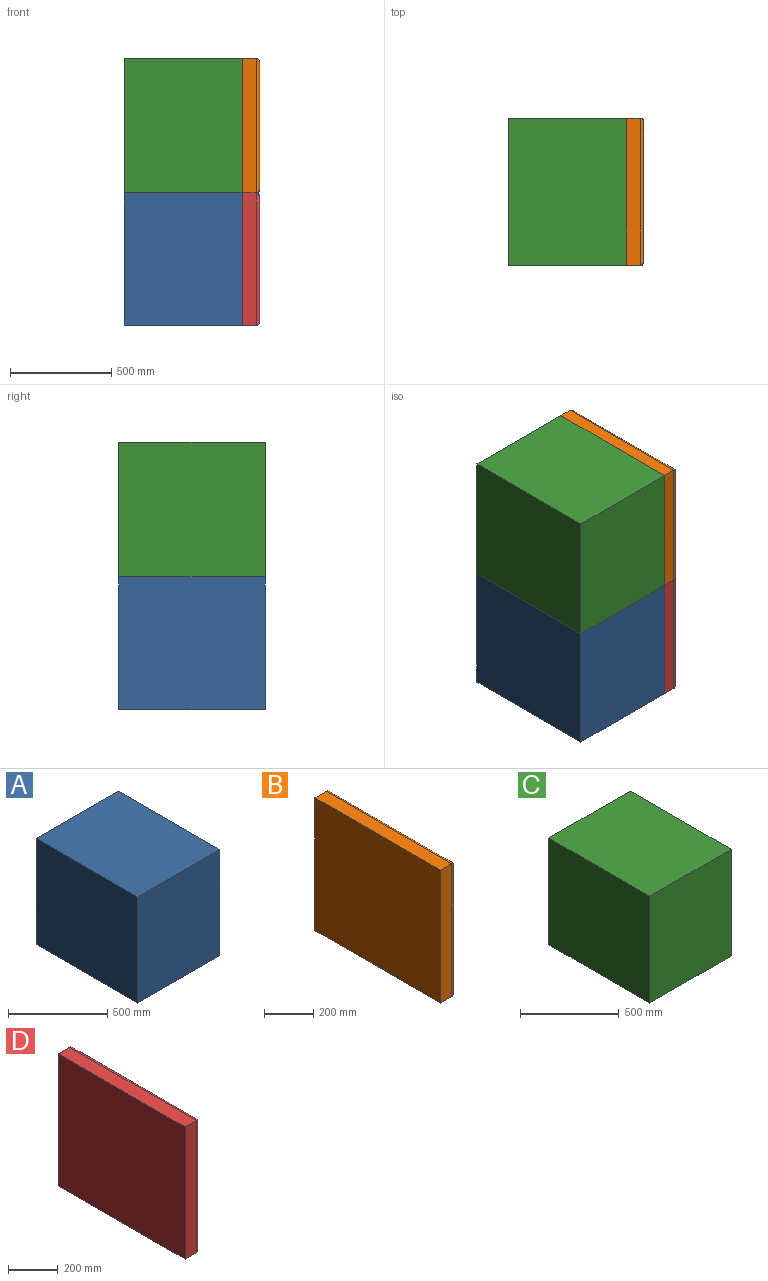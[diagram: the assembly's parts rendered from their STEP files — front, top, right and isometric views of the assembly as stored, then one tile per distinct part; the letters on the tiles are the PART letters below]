
ASSEMBLY  parts=4 mates=2
PART A: 11 faces, bbox 584.2x723.9x653.2 mm
  f0: plane 723.9x653.25mm, normal (1,0,0), area 129595.5mm2, adj f1,f2,f3,f4,f6,f7,f8,f9
  f1: plane 653.25x584.2mm, normal (0,1,0), area 381626.4mm2, adj f0,f2,f4,f5
  f2: plane 723.9x584.2mm, normal (0,0,1), area 422902.4mm2, adj f0,f1,f3,f5
  f3: plane 653.25x584.2mm, normal (0,-1,0), area 381626.4mm2, adj f0,f2,f4,f5
  f4: plane 723.9x584.2mm, normal (0,0,-1), area 422902.4mm2, adj f0,f1,f3,f5
  f5: plane 723.9x653.25mm, normal (-1,0,0), area 472884.9mm2, adj f1,f2,f3,f4
  f6: plane 551.65x533.4mm, normal (0,-1,0), area 294248.1mm2, adj f0,f7,f9,f10
  f7: plane 622.3x533.4mm, normal (0,0,-1), area 331934.8mm2, adj f0,f6,f8,f10
  f8: plane 551.65x533.4mm, normal (0,1,0), area 294248.1mm2, adj f0,f7,f9,f10
  f9: plane 622.3x533.4mm, normal (0,0,1), area 331934.8mm2, adj f0,f6,f8,f10
  f10: plane 622.3x551.65mm, normal (1,0,0), area 343289.4mm2, adj f6,f7,f8,f9
PART B: 10 faces, bbox 82.6x723.9x662.8 mm
  f0: plane 723.9x64.77mm, normal (0,0,-1), area 46887mm2, adj f1,f3,f5,f6
  f1: plane 662.79x64.77mm, normal (0,1,0), area 42929mm2, adj f0,f2,f5,f7
  f2: plane 723.9x64.77mm, normal (0,0,1), area 46887mm2, adj f1,f3,f5,f9
  f3: plane 662.79x64.77mm, normal (0,-1,0), area 42929mm2, adj f0,f2,f5,f8
  f4: plane 688.34x627.23mm, normal (1,0,0), area 431748.4mm2, adj f6,f7,f8,f9
  f5: plane 723.9x662.79mm, normal (-1,0,0), area 479794.7mm2, adj f0,f1,f2,f3
  f6: cylinder r=17.78mm len=723.9mm, axis (0,-1,0), area 19856.7mm2, adj f0,f4,f7,f8
  f7: cylinder r=17.78mm len=662.79mm, axis (0,0,-1), area 18150mm2, adj f1,f4,f6,f9
  f8: cylinder r=17.78mm len=662.79mm, axis (0,0,1), area 18150mm2, adj f3,f4,f6,f9
  f9: cylinder r=17.78mm len=723.9mm, axis (0,1,0), area 19856.7mm2, adj f2,f4,f7,f8
PART C: 11 faces, bbox 584.2x723.9x662.8 mm
  f0: plane 723.9x662.79mm, normal (1,0,0), area 130565.3mm2, adj f1,f2,f3,f4,f6,f7,f8,f9
  f1: plane 723.9x584.2mm, normal (0,0,-1), area 422902.4mm2, adj f0,f2,f4,f5
  f2: plane 662.79x584.2mm, normal (0,1,0), area 387202.7mm2, adj f0,f1,f3,f5
  f3: plane 723.9x584.2mm, normal (0,0,1), area 422902.4mm2, adj f0,f2,f4,f5
  f4: plane 662.79x584.2mm, normal (0,-1,0), area 387202.7mm2, adj f0,f1,f3,f5
  f5: plane 723.9x662.79mm, normal (-1,0,0), area 479794.7mm2, adj f1,f2,f3,f4
  f6: plane 622.3x533.4mm, normal (0,0,1), area 331934.8mm2, adj f0,f7,f9,f10
  f7: plane 561.19x533.4mm, normal (0,-1,0), area 299339.5mm2, adj f0,f6,f8,f10
  f8: plane 622.3x533.4mm, normal (0,0,-1), area 331934.8mm2, adj f0,f7,f9,f10
  f9: plane 561.19x533.4mm, normal (0,1,0), area 299339.5mm2, adj f0,f6,f8,f10
  f10: plane 622.3x561.19mm, normal (1,0,0), area 349229.4mm2, adj f6,f7,f8,f9
PART D: 10 faces, bbox 82.6x723.9x653.2 mm
  f0: plane 653.25x64.77mm, normal (0,1,0), area 42310.8mm2, adj f1,f3,f5,f6
  f1: plane 723.9x64.77mm, normal (0,0,1), area 46887mm2, adj f0,f2,f5,f7
  f2: plane 653.25x64.77mm, normal (0,-1,0), area 42310.8mm2, adj f1,f3,f5,f9
  f3: plane 723.9x64.77mm, normal (0,0,-1), area 46887mm2, adj f0,f2,f5,f8
  f4: plane 688.34x617.69mm, normal (1,0,0), area 425178.1mm2, adj f6,f7,f8,f9
  f5: plane 723.9x653.25mm, normal (-1,0,0), area 472884.9mm2, adj f0,f1,f2,f3
  f6: cylinder r=17.78mm len=653.25mm, axis (0,0,-1), area 17883.5mm2, adj f0,f4,f7,f8
  f7: cylinder r=17.78mm len=723.9mm, axis (0,1,0), area 19856.7mm2, adj f1,f4,f6,f9
  f8: cylinder r=17.78mm len=723.9mm, axis (0,-1,0), area 19856.7mm2, adj f3,f4,f6,f9
  f9: cylinder r=17.78mm len=653.25mm, axis (0,0,1), area 17883.5mm2, adj f2,f4,f7,f8
PLACE A at identity fixed
PLACE B at identity
PLACE C at identity
PLACE D rot(axis=(0,1,0),0deg) t=(0,0,0)mm
MATE revolute A.f3 <-> D.f2  axis (0,-1,0) through (-1346.2,469.9,431.8)mm
MATE revolute C.f4 <-> B.f3  axis (0,-1,0) through (-1346.2,469.9,1085.05)mm
